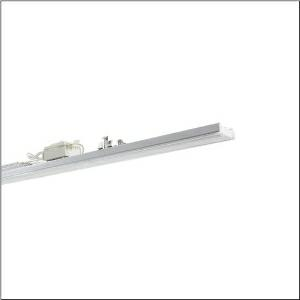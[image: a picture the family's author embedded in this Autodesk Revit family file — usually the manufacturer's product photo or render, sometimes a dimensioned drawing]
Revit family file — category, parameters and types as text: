
# Revit family: licross_11_recessed_ho_51tl1edv4m1s
name_source: partatom
category: Lighting Fixtures
units: mm (PartAtom-declared; Revit-internal decimal feet)

## family parameters
Cut with Voids When Loaded = No
Host = Face
Light Source = No
Part Type = Normal
Room Calculation Point = No
Round Connector Dimension = Use Diameter
Shared = No

## types (1)
- --- (1 x LED, 26450 lm, 150.5 W, 4000K)
    Apparent Load = 150 VA
    CIE Flux Codes = 85 95 99 100 100
    Color Rendering = 80
    Color Temperature = 4000K
    Default Elevation = 1800 mm
    Description = Licross 11 Recessed HO, luminaire insert, of sheet steel, coil coated, white, length: 2.250mm, width: 66mm, height: 67mm, LED rated luminous flux: 26.450lm, light colour: 840, SDCM (Standard Deviation of Colour Matching)MacAdam ≤ 2 SDCM (initial), control gear: DALI 2, with plug, 5-pole, with phase selection, mains connection: 220..240V, AC, 50/60Hz, rated input power: 151W, internal wiring halogen-free, primary light control with lens, of plastic, primary optical cover: cover, of PMMA, light emission: direct distribution, primary light characteristic: symmetric, protection rating (complete): IP40, insulation class (complete): insulation class I (protective earthing), certification: CE, ENEC, VDE, UKCA, protection symbol: D if used in an environment without relevant dust loads with corresponding accessories, impact resistance: IK06, permissible ambient temperature for indoor applications: -40..+35°C, corresponds to IFS (International Featured Standards) requirements for safety and quality in the food industry, reducing of maximum allowable ambient temperature of 5°C with ceiling mounting, LABS conformity tested according to VDMA 24364:2018-05, The light source and the operating device comply with the requirements of the Ecodesign Regulation (EU) 2019/2020 and are replaceable in accordance with this regulation, packaging unit: 1 piece
    Height = 58 mm
    Lamp = 1 x LED
    Lamp Light Flux = 26450 lm
    Lamp Power = 150.5 W
    Lamp count = 1
    Length = 2250 mm
    Luminous efficacy = 176 lm/W
    Manufacturer = Siteco
    ModVariant = No
    Model = 51TL1EDV4M1S
    Mounting Place = Ceiling
    Mounting Type = Pendant
    Number of Poles = 1
    OnlyDefault = Yes
    Power Factor = 1
    Product Name = Licross 11 Recessed HO
    Product group = luminaire insert | ceiling pendant
    ProductGroupID = 901
    Protection Class = Protection class I
    Protection Degree = IP 40
    RLX_Detail_Level = 1
    RLX_Emergency_Light_Flux = 0 lm
    RLX_Emergency_Type = 0
    RLX_Emergency_Type_DB = No
    RlxData = <blob elided: 29993 chars, md5=b88778f5>
    Socket = socket
    Standby Power = 0 W
    System Light Flux = 26450 lm
    System Power = 150 W
    Type Comments = factory setting: luminous flux: 100 % | dim-lin: 254 | 690 mA
    Type Image = l_1296930.jpg
    URL = http://relux.com
    VarID = @adj_099687
    Voltage = 0 V
    Weight = 0.00 kg
    Width = 66 mm

## geometry (parser evidence)
native form markers: Blend x4, Sweep x10
no freeform markers — native parametric forms only
